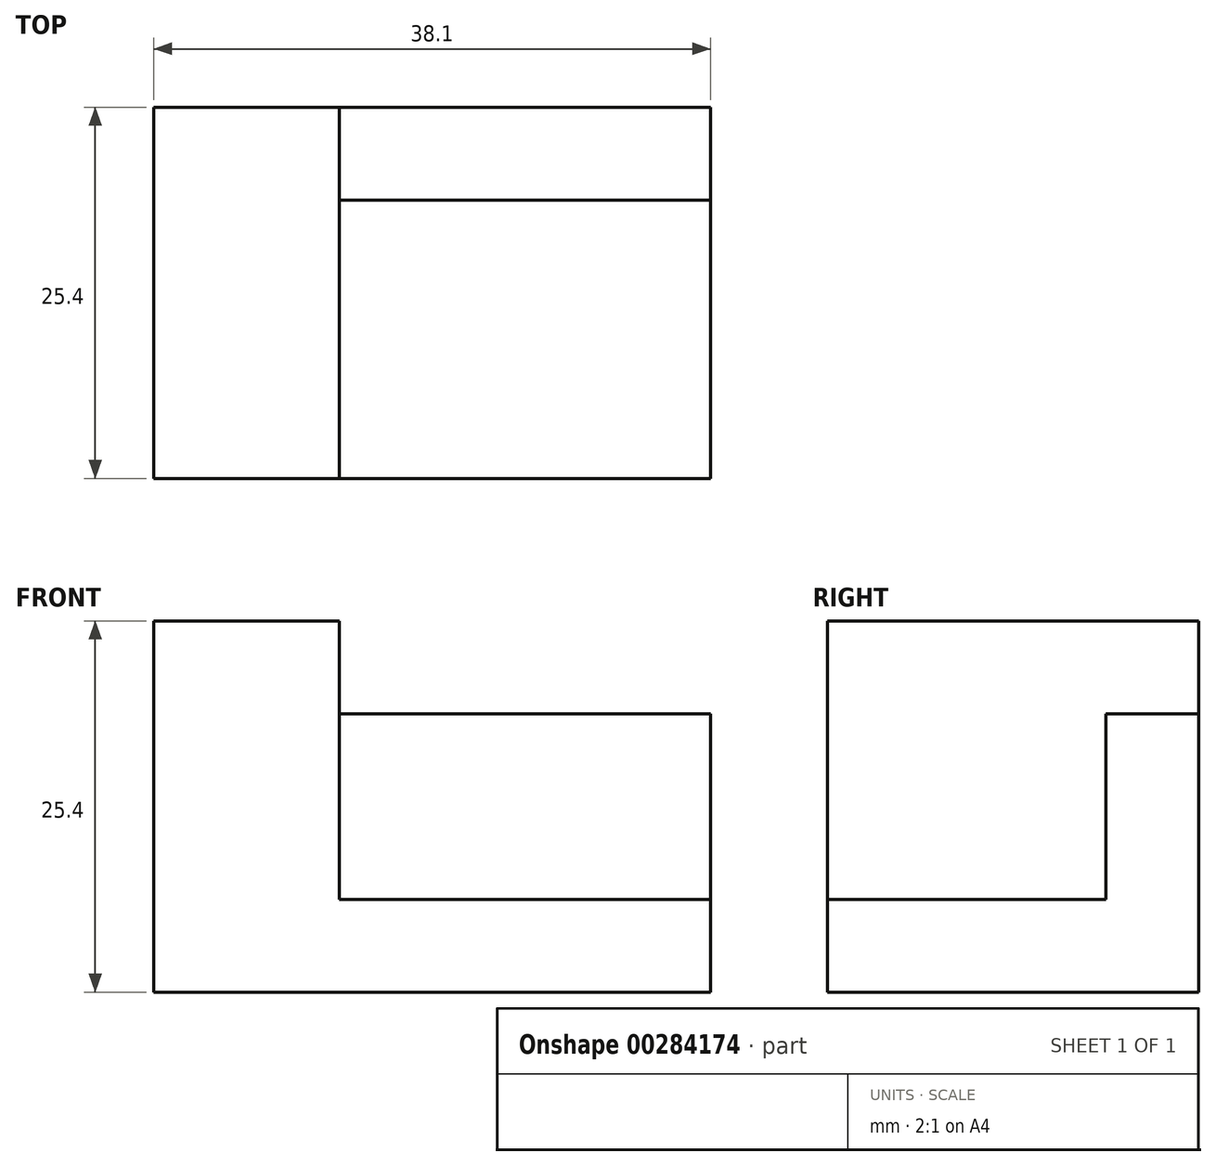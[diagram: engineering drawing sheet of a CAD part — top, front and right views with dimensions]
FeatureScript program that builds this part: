
annotation { "Feature Type Name" : "Feature", "Feature Type Description" : "" }
export const myFeature = defineFeature(function(context is Context, id is Id, definition is map)
    precondition{}
    {
        {
            var Q0;
            Q0=qCreatedBy(makeId("Front.planeOp"),FACE);
            var sketch = newSketch(context, id + "F0", { "sketchPlane" : qUnion([Q0])});
            skLineSegment(sketch, "E0", {"start": v(0, 0) * mm, "end": v(38.1, 0) * mm});
            skLineSegment(sketch, "E1", {"start": v(0, 0) * mm, "end": v(0, 25.4) * mm});
            skLineSegment(sketch, "E2", {"start": v(0, 25.4) * mm, "end": v(12.7, 25.4) * mm});
            skLineSegment(sketch, "E3", {"start": v(12.7, 25.4) * mm, "end": v(12.7, 6.35) * mm});
            skLineSegment(sketch, "E4", {"start": v(12.7, 6.35) * mm, "end": v(38.1, 6.35) * mm});
            skLineSegment(sketch, "E5", {"start": v(38.1, 6.35) * mm, "end": v(38.1, 0) * mm});
            skLineSegment(sketch, "E6.bottom", {"start": v(12.7, 19.05) * mm, "end": v(38.1, 19.05) * mm});
            skLineSegment(sketch, "E6.left", {"start": v(12.7, 19.05) * mm, "end": v(12.7, 6.35) * mm});
            skLineSegment(sketch, "E6.right", {"start": v(38.1, 19.05) * mm, "end": v(38.1, 6.35) * mm});
            skSolve(sketch);
        }
        {
            var Q0;
            Q0=makeQuery(id+"F0.imprint","IMPRINT",FACE,{"disambiguationData":[TD([[makeQuery(id+"F0.imprint","IMPRINT",EDGE,{"derivedFrom":sQuery(id+"F0.wireOp",EDGE,"E0")}),1.0]])]});
            extrude(context, id + "F1", {"entities" : qUnion([Q0]), "endBound" : BoundingType.SYMMETRIC, "depth" : 25.4 * mm});
        }
        {
            var Q0;
            Q0=makeQuery(id+"F0.imprint","IMPRINT",FACE,{"disambiguationData":[TD([[makeQuery(id+"F0.imprint","IMPRINT",EDGE,{"derivedFrom":sQuery(id+"F0.wireOp",EDGE,"E6.bottom")}),-1.0]])]});
            extrude(context, id + "F2", {"entities" : qUnion([Q0]), "operationType" : NewBodyOperationType.ADD, "oppositeDirection" : true, "depth" : 12.7 * mm});
        }
        {
            var Q0;
            Q0=makeQuery(id+"F0.imprint","IMPRINT",FACE,{"disambiguationData":[TD([[makeQuery(id+"F0.imprint","IMPRINT",EDGE,{"derivedFrom":sQuery(id+"F0.wireOp",EDGE,"E6.bottom")}),-1.0]])]});
            extrude(context, id + "F3", {"entities" : qUnion([Q0]), "operationType" : NewBodyOperationType.REMOVE, "oppositeDirection" : true, "depth" : 6.35 * mm});
        }
    });
